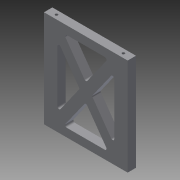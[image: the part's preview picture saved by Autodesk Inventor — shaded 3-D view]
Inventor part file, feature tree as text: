
AUTODESK INVENTOR PART (.ipt)
format: ipt  version: 2013 (Build 170138000, 138)  size: 140,288 bytes
history: native  units: mm
features: sketch x3, extrude x2, hole x1, fillet x1
ambient origin geometry x8: Origin, YZ Plane, XZ Plane, XY Plane, X Axis, Y Axis, Z Axis, Center Point
feature tree (7):
  extrude  "押し出し2"  Depth=50.0mm
  hole  "穴1"  [1 undecoded]
  extrude  "押し出し3"  Depth=25.0mm
  fillet  "フィレット1"  Radius=5.0mm
  sketch  "スケッチ1"
  sketch  "スケッチ2"
  sketch  "スケッチ3"
note: 1 required parameter value undecoded (feature->parameter linkage not recoverable at this tier; creation-order binding heuristic only, values carry confidence <= 0.55)
